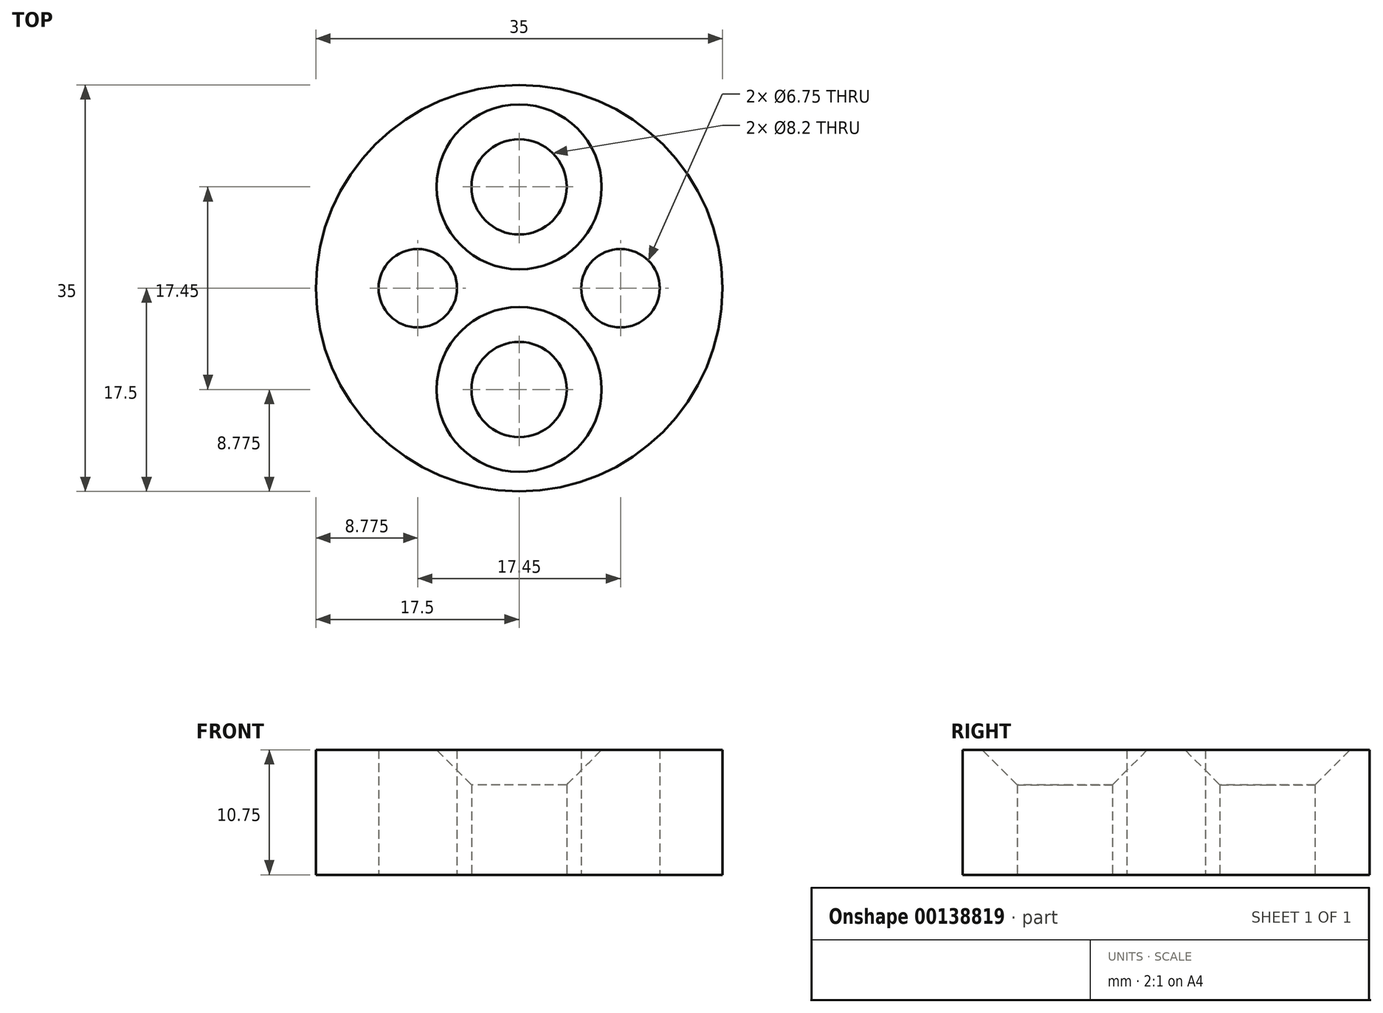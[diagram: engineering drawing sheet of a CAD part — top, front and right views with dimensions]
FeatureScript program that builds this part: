
annotation { "Feature Type Name" : "Feature", "Feature Type Description" : "" }
export const myFeature = defineFeature(function(context is Context, id is Id, definition is map)
    precondition{}
    {
        {
            var Q0;
            Q0=qCreatedBy(makeId("Top.planeOp"),FACE);
            var sketch = newSketch(context, id + "F0", { "sketchPlane" : qUnion([Q0])});
            skCircle(sketch, "E0", {"center": v(0, 0) * mm, "radius": 17.5 * mm});
            skCircle(sketch, "E1", {"center": v(-8.72, 0) * mm, "radius": 3.38 * mm});
            skCircle(sketch, "E2.MirrorC", {"center": v(8.72, 0) * mm, "radius": 3.38 * mm});
            skCircle(sketch, "E3", {"center": v(0, 8.72) * mm, "radius": 4.1 * mm});
            skCircle(sketch, "E4.MirrorC", {"center": v(0, -8.72) * mm, "radius": 4.1 * mm});
            skSolve(sketch);
        }
        {
            var Q0;
            Q0=makeQuery(id+"F0.imprint","IMPRINT",FACE,{"disambiguationData":[TD([[makeQuery(id+"F0.imprint","IMPRINT",EDGE,{"derivedFrom":sQuery(id+"F0.wireOp",EDGE,"E0")}),1.0]])]});
            extrude(context, id + "F1", {"entities" : qUnion([Q0]), "depth" : 10.75 * mm});
        }
        {
            var Q0;
            Q0=makeQuery(id+"F1.opExtrude","CAP_EDGE",EDGE,{"disambiguationData":[OSD([sQuery(id+"F0.wireOp",EDGE,"E3")])],"isStart":false});
            var Q1;
            Q1=makeQuery(id+"F1.opExtrude","CAP_EDGE",EDGE,{"disambiguationData":[OSD([sQuery(id+"F0.wireOp",EDGE,"E4.MirrorC")])],"isStart":false});
            chamfer(context, id + "F2", {"entities" : qUnion([Q0, Q1]), "width" : 3 * mm, "tangentPropagation" : true});
        }
    });
